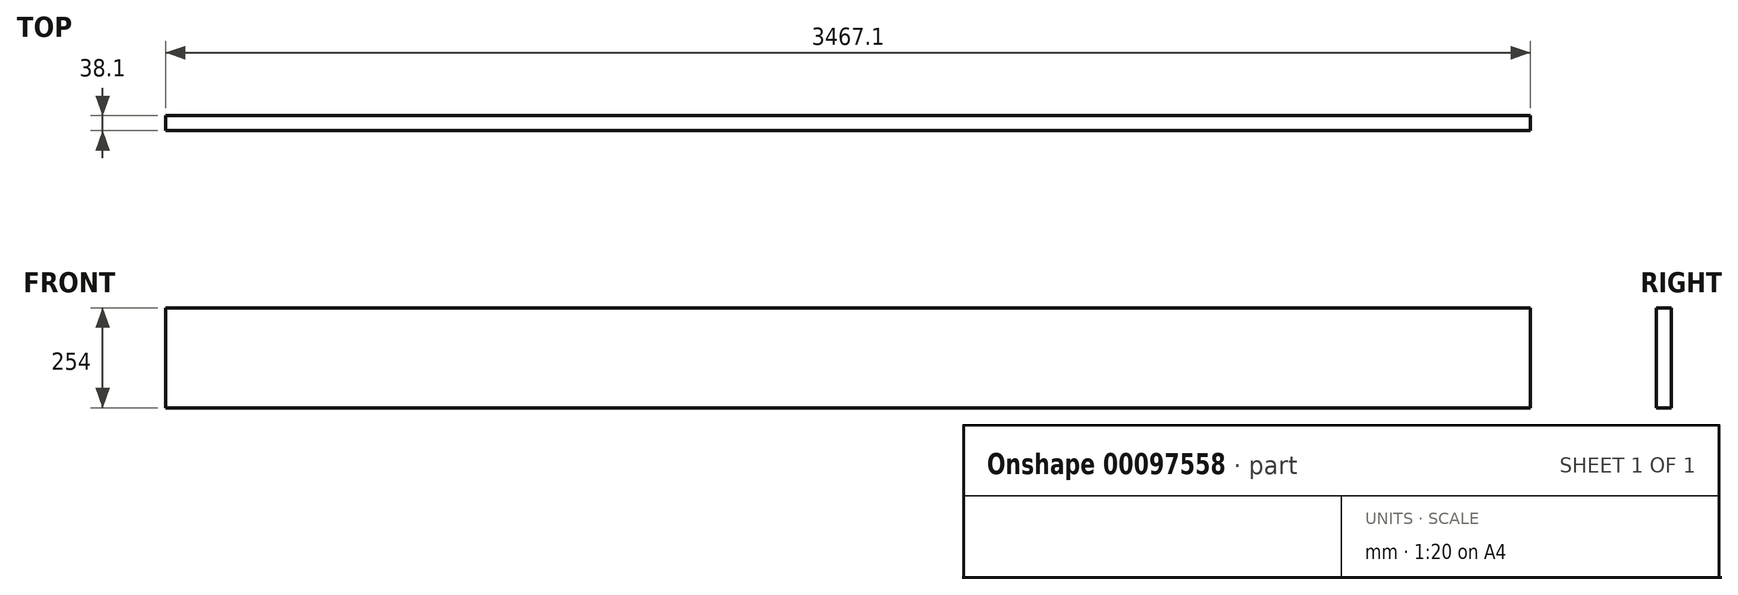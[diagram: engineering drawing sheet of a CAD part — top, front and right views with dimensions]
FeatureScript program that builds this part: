
annotation { "Feature Type Name" : "Feature", "Feature Type Description" : "" }
export const myFeature = defineFeature(function(context is Context, id is Id, definition is map)
    precondition{}
    {
        {
            var Q0;
            Q0=qCreatedBy(makeId("Front.planeOp"),FACE);
            var sketch = newSketch(context, id + "F0", { "sketchPlane" : qUnion([Q0])});
            skLineSegment(sketch, "E0.bottom", {"start": v(1733.55, 127) * mm, "end": v(-1733.55, 127) * mm});
            skLineSegment(sketch, "E0.top", {"start": v(1733.55, -127) * mm, "end": v(-1733.55, -127) * mm});
            skLineSegment(sketch, "E0.left", {"start": v(1733.55, 127) * mm, "end": v(1733.55, -127) * mm});
            skLineSegment(sketch, "E0.right", {"start": v(-1733.55, 127) * mm, "end": v(-1733.55, -127) * mm});
            skPoint(sketch, "E0.middle", {"position": v(0, 0) * mm});
            skSolve(sketch);
        }
        {
            var Q0;
            Q0=makeQuery(id+"F0.imprint","IMPRINT",FACE,{"disambiguationData":[TD([[makeQuery(id+"F0.imprint","IMPRINT",EDGE,{"derivedFrom":sQuery(id+"F0.wireOp",EDGE,"E0.bottom")}),1.0]])]});
            extrude(context, id + "F1", {"entities" : qUnion([Q0]), "depth" : 38.1 * mm});
        }
    });
